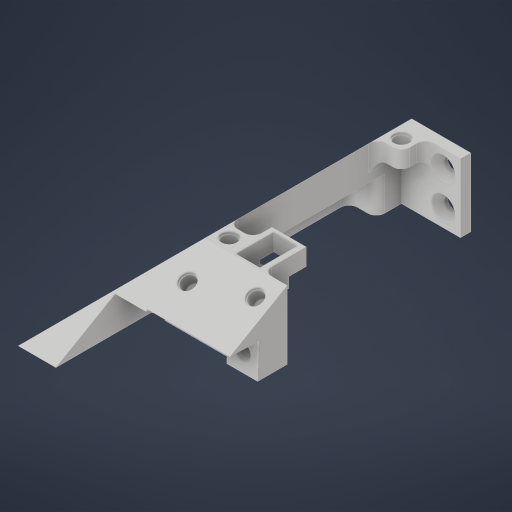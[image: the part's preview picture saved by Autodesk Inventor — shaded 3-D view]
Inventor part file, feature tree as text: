
AUTODESK INVENTOR PART (.ipt)
format: ipt  version: 2023 (Build 270158000, 158)  size: 499,712 bytes
history: native  units: mm
features: sketch x19, extrude x14, hole x6, other x2, mirror x1, fillet x1
ambient origin geometry x8: Origin, YZ Plane, XZ Plane, XY Plane, X Axis, Y Axis, Z Axis, Center Point
bodies: Body1 (feature_tree), Body2 (feature_tree)
feature tree (43):
  other  "Bryła1"
  extrude  "Wyciągnięcie proste1"  Depth=95.0mm
  extrude  "Wyciągnięcie proste2"  Depth=20.0mm
  extrude  "Wyciągnięcie proste3"  Depth=20.0mm TaperAngle=0.0deg
  extrude  "Wyciągnięcie proste4"  TaperAngle=45.0deg  [1 undecoded]
  extrude  "Wyciągnięcie proste5"  Depth=20.0mm TaperAngle=0.0deg
  extrude  "Wyciągnięcie proste6"  TaperAngle=30.0deg  [1 undecoded]
  extrude  "Wyciągnięcie proste7"  Depth=20.0mm TaperAngle=0.0deg
  hole  "Otwór1"  [1 undecoded]
  extrude  "Wyciągnięcie proste8"  Depth=9.0mm
  extrude  "Wyciągnięcie proste9"  Depth=24.0mm TaperAngle=0.0deg
  extrude  "Wyciągnięcie proste10"  Depth=9.0mm
  hole  "Otwór2"  [1 undecoded]
  hole  "Otwór3"  [1 undecoded]
  other  "Płaszczyzna konstrukcyjna1"
  extrude  "Wyciągnięcie proste13"  Depth=1.5mm TaperAngle=0.0deg
  hole  "Otwór4"  [1 undecoded]
  hole  "Otwór5"  [1 undecoded]
  mirror  "Odbij1"
  extrude  "Wyciągnięcie proste14"  Depth=15.358897mm
  extrude  "Wyciągnięcie proste15"  Depth=20.0mm TaperAngle=0.0deg
  extrude  "Wyciągnięcie proste16"  Depth=65.0mm
  hole  "Otwór6"  [1 undecoded]
  fillet  "Fillet1"  Radius=5.0mm
  sketch  "Szkic1"
  sketch  "Szkic2"
  sketch  "Szkic3"
  sketch  "Szkic4"
  sketch  "Szkic5"
  sketch  "Szkic6"
  sketch  "Szkic7"
  sketch  "Szkic8"
  sketch  "Szkic9"
  sketch  "Szkic11"
  sketch  "Szkic12"
  sketch  "Szkic13"
  sketch  "Szkic14"
  sketch  "Szkic17"
  sketch  "Szkic18"
  sketch  "Szkic20"
  sketch  "Szkic21"
  sketch  "Szkic22"
  sketch  "Szkic23"
note: 8 required parameter values undecoded (feature->parameter linkage not recoverable at this tier; creation-order binding heuristic only, values carry confidence <= 0.55)
